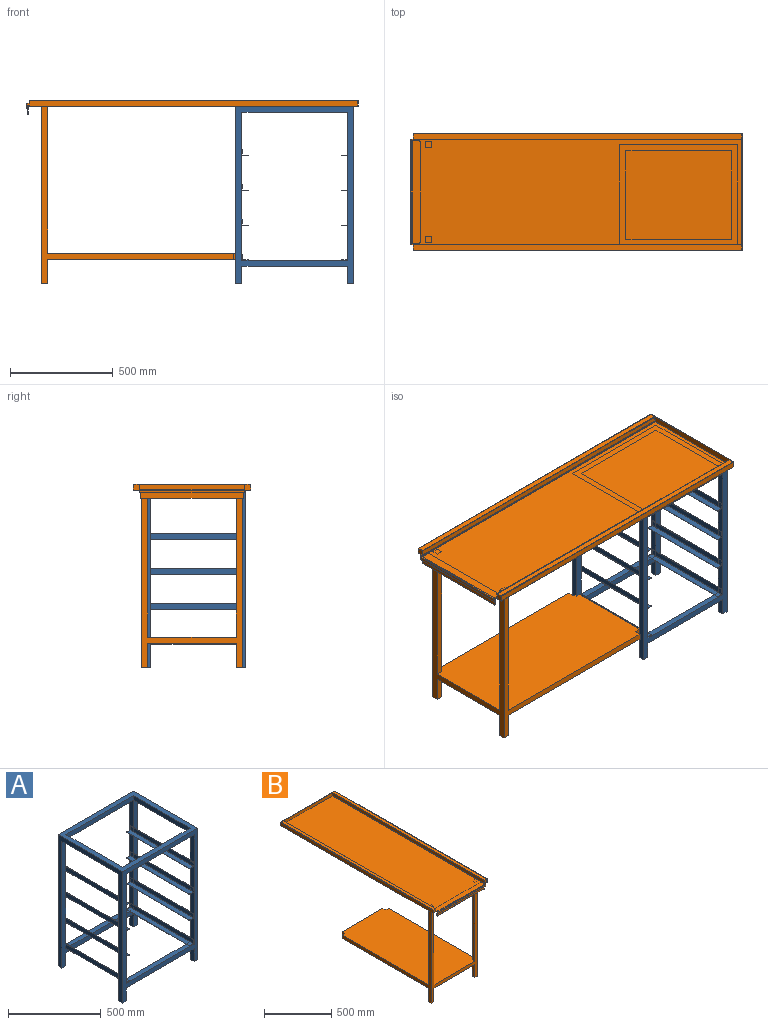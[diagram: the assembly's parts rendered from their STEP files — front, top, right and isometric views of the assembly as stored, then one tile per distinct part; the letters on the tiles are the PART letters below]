
ASSEMBLY  parts=2 mates=1
PART A: 127 faces, bbox 575x490x865 mm
  f0: plane 720x30mm, normal (-1,0,0), area 18621.5mm2, adj f3,f18,f20,f26,f82,f84,f90,f93
  f1: plane 515x30mm, normal (0,0,1), area 13960.7mm2, adj f5,f6,f8,f12,f35,f38,f39,f83
  f2: plane 720x30mm, normal (1,0,0), area 18621.5mm2, adj f3,f18,f20,f26,f34,f36,f42,f45
  f3: plane 515x30mm, normal (0,0,1), area 13960.7mm2, adj f0,f2,f18,f20,f36,f38,f40,f84
  f4: plane 515x30mm, normal (0,1,0), area 15450mm2, adj f10,f17,f28,f29
  f5: plane 835x575mm, normal (0,1,0), area 65550mm2, adj f1,f6,f7,f9,f11,f12,f13,f14
  f6: plane 720x30mm, normal (1,0,0), area 18621.5mm2, adj f1,f5,f8,f17,f34,f35,f41,f45
  f7: plane 865x490mm, normal (-1,0,0), area 64800mm2, adj f5,f8,f10,f11,f18,f20,f22,f27
  f8: plane 865x575mm, normal (0,-1,0), area 82800mm2, adj f1,f6,f7,f9,f10,f11,f12,f13
  f9: plane 85x30mm, normal (1,0,0), area 2550mm2, adj f5,f8,f11,f16
  f10: plane 575x490mm, normal (0,0,1), area 60300mm2, adj f4,f7,f8,f13,f20,f21,f28,f29
  f11: plane 30x30mm, normal (0,0,-1), area 900mm2, adj f5,f7,f8,f9
  f12: plane 720x30mm, normal (-1,0,0), area 18621.5mm2, adj f1,f5,f8,f17,f82,f83,f89,f93
  f13: plane 865x490mm, normal (1,0,0), area 64800mm2, adj f5,f8,f10,f15,f18,f20,f24,f30
  f14: plane 85x30mm, normal (-1,0,0), area 2550mm2, adj f5,f8,f15,f16
  f15: plane 30x30mm, normal (0,0,-1), area 900mm2, adj f5,f8,f13,f14
  f16: plane 515x30mm, normal (0,0,-1), area 15450mm2, adj f5,f8,f9,f14
  f17: plane 515x30mm, normal (0,0,-1), area 15450mm2, adj f4,f6,f8,f12
  f18: plane 835x575mm, normal (0,-1,0), area 65550mm2, adj f0,f2,f3,f7,f13,f19,f22,f23
  f19: plane 85x30mm, normal (1,0,0), area 2550mm2, adj f18,f20,f22,f25
  f20: plane 865x575mm, normal (0,1,0), area 82800mm2, adj f0,f2,f3,f7,f10,f13,f19,f22
  f21: plane 515x30mm, normal (0,-1,0), area 15450mm2, adj f10,f26,f28,f29
  f22: plane 30x30mm, normal (0,0,-1), area 900mm2, adj f7,f18,f19,f20
  f23: plane 85x30mm, normal (-1,0,0), area 2550mm2, adj f18,f20,f24,f25
  f24: plane 30x30mm, normal (0,0,-1), area 900mm2, adj f13,f18,f20,f23
  f25: plane 515x30mm, normal (0,0,-1), area 15450mm2, adj f18,f19,f20,f23
  f26: plane 515x30mm, normal (0,0,-1), area 15450mm2, adj f0,f2,f20,f21
  f27: plane 430x30mm, normal (0,0,-1), area 12900mm2, adj f5,f7,f18,f28
  f28: plane 430x30mm, normal (1,0,0), area 12900mm2, adj f4,f10,f21,f27
  f29: plane 430x30mm, normal (-1,0,0), area 12900mm2, adj f4,f10,f21,f30
  f30: plane 430x30mm, normal (0,0,-1), area 12900mm2, adj f5,f13,f18,f29
  f31: plane 430x30mm, normal (0,0,-1), area 12900mm2, adj f5,f18,f32,f38
  f32: plane 430x30mm, normal (-1,0,0), area 12900mm2, adj f5,f18,f31,f34
  f33: plane 480x28.5mm, normal (1,0,0), area 13669.3mm2, adj f34,f35,f36,f37,f41,f42
  f34: plane 470x1.5mm, normal (0,0,1), area 705mm2, adj f2,f6,f32,f33,f41,f42
  f35: plane 25x25mm, normal (0,-1,0), area 72.8mm2, adj f1,f6,f33,f37,f39,f41
  f36: plane 25x25mm, normal (0,1,0), area 72.8mm2, adj f2,f3,f33,f37,f40,f42
  f37: plane 480x28.5mm, normal (0,0,1), area 13669.3mm2, adj f33,f35,f36,f38,f39,f40
  f38: plane 470x1.5mm, normal (1,0,0), area 705mm2, adj f1,f3,f31,f37,f39,f40
  f39: cylinder r=5mm len=5mm, axis (0,0,1), area 11.8mm2, adj f1,f35,f37,f38
  f40: cylinder r=5mm len=5mm, axis (0,0,-1), area 11.8mm2, adj f3,f36,f37,f38
  f41: cylinder r=5mm len=5mm, axis (-1,0,0), area 11.8mm2, adj f6,f33,f34,f35
  f42: cylinder r=5mm len=5mm, axis (1,0,0), area 11.8mm2, adj f2,f33,f34,f36
  f43: plane 430x30mm, normal (-1,0,0), area 12900mm2, adj f5,f18,f45,f47
  f44: plane 480x28.5mm, normal (1,0,0), area 13669.3mm2, adj f45,f46,f48,f49,f53,f54
  f45: plane 470x1.5mm, normal (0,0,1), area 705mm2, adj f2,f6,f43,f44,f53,f54
  f46: plane 25x25mm, normal (0,-1,0), area 72.8mm2, adj f6,f44,f47,f49,f52,f54
  f47: plane 480x30mm, normal (0,0,-1), area 14389.3mm2, adj f2,f6,f43,f46,f48,f50,f51,f52
  f48: plane 25x25mm, normal (0,1,0), area 72.8mm2, adj f2,f44,f47,f49,f51,f53
  f49: plane 480x28.5mm, normal (0,0,1), area 13669.3mm2, adj f44,f46,f48,f50,f51,f52
  f50: plane 470x1.5mm, normal (1,0,0), area 705mm2, adj f47,f49,f51,f52
  f51: cylinder r=5mm len=5mm, axis (0,0,-1), area 11.8mm2, adj f47,f48,f49,f50
  f52: cylinder r=5mm len=5mm, axis (0,0,1), area 11.8mm2, adj f46,f47,f49,f50
  f53: cylinder r=5mm len=5mm, axis (1,0,0), area 11.8mm2, adj f2,f44,f45,f48
  f54: cylinder r=5mm len=5mm, axis (-1,0,0), area 11.8mm2, adj f6,f44,f45,f46
  f55: plane 430x30mm, normal (-1,0,0), area 12900mm2, adj f5,f18,f57,f59
  f56: plane 480x28.5mm, normal (1,0,0), area 13669.3mm2, adj f57,f58,f60,f61,f65,f66
  f57: plane 470x1.5mm, normal (0,0,1), area 705mm2, adj f2,f6,f55,f56,f65,f66
  f58: plane 25x25mm, normal (0,-1,0), area 72.8mm2, adj f6,f56,f59,f61,f64,f65
  f59: plane 480x30mm, normal (0,0,-1), area 14389.3mm2, adj f2,f6,f55,f58,f60,f62,f63,f64
  f60: plane 25x25mm, normal (0,1,0), area 72.8mm2, adj f2,f56,f59,f61,f63,f66
  f61: plane 480x28.5mm, normal (0,0,1), area 13669.3mm2, adj f56,f58,f60,f62,f63,f64
  f62: plane 470x1.5mm, normal (1,0,0), area 705mm2, adj f59,f61,f63,f64
  f63: cylinder r=5mm len=5mm, axis (0,0,-1), area 11.8mm2, adj f59,f60,f61,f62
  f64: cylinder r=5mm len=5mm, axis (0,0,1), area 11.8mm2, adj f58,f59,f61,f62
  f65: cylinder r=5mm len=5mm, axis (-1,0,0), area 11.8mm2, adj f6,f56,f57,f58
  f66: cylinder r=5mm len=5mm, axis (1,0,0), area 11.8mm2, adj f2,f56,f57,f60
  f67: plane 430x30mm, normal (-1,0,0), area 12900mm2, adj f5,f18,f69,f71
  f68: plane 480x28.5mm, normal (1,0,0), area 13669.3mm2, adj f69,f70,f72,f73,f77,f78
  f69: plane 470x1.5mm, normal (0,0,1), area 705mm2, adj f2,f6,f67,f68,f77,f78
  f70: plane 25x25mm, normal (0,-1,0), area 72.7mm2, adj f6,f68,f71,f73,f76,f77
  f71: plane 480x30mm, normal (0,0,-1), area 14389.3mm2, adj f2,f6,f67,f70,f72,f74,f75,f76
  f72: plane 25x25mm, normal (0,1,0), area 72.7mm2, adj f2,f68,f71,f73,f75,f78
  f73: plane 480x28.5mm, normal (0,0,1), area 13669.3mm2, adj f68,f70,f72,f74,f75,f76
  f74: plane 470x1.5mm, normal (1,0,0), area 705mm2, adj f71,f73,f75,f76
  f75: cylinder r=5mm len=5mm, axis (0,0,-1), area 11.8mm2, adj f71,f72,f73,f74
  f76: cylinder r=5mm len=5mm, axis (0,0,1), area 11.8mm2, adj f70,f71,f73,f74
  f77: cylinder r=5mm len=5mm, axis (-1,0,0), area 11.8mm2, adj f6,f68,f69,f70
  f78: cylinder r=5mm len=5mm, axis (1,0,0), area 11.8mm2, adj f2,f68,f69,f72
  f79: plane 430x30mm, normal (0,0,-1), area 12900mm2, adj f5,f18,f80,f86
  f80: plane 430x30mm, normal (1,0,0), area 12900mm2, adj f5,f18,f79,f82
  f81: plane 480x28.5mm, normal (-1,0,0), area 13669.3mm2, adj f82,f83,f84,f85,f89,f90
  f82: plane 470x1.5mm, normal (0,0,1), area 705mm2, adj f0,f12,f80,f81,f89,f90
  f83: plane 25x25mm, normal (0,-1,0), area 72.8mm2, adj f1,f12,f81,f85,f87,f89
  f84: plane 25x25mm, normal (0,1,0), area 72.8mm2, adj f0,f3,f81,f85,f88,f90
  f85: plane 480x28.5mm, normal (0,0,1), area 13669.3mm2, adj f81,f83,f84,f86,f87,f88
  f86: plane 470x1.5mm, normal (-1,0,0), area 705mm2, adj f1,f3,f79,f85,f87,f88
  f87: cylinder r=5mm len=5mm, axis (0,0,1), area 11.8mm2, adj f1,f83,f85,f86
  f88: cylinder r=5mm len=5mm, axis (0,0,-1), area 11.8mm2, adj f3,f84,f85,f86
  f89: cylinder r=5mm len=5mm, axis (1,0,0), area 11.8mm2, adj f12,f81,f82,f83
  f90: cylinder r=5mm len=5mm, axis (-1,0,0), area 11.8mm2, adj f0,f81,f82,f84
  f91: plane 430x30mm, normal (1,0,0), area 12900mm2, adj f5,f18,f93,f95
  f92: plane 480x28.5mm, normal (-1,0,0), area 13669.3mm2, adj f93,f94,f96,f97,f101,f102
  f93: plane 470x1.5mm, normal (0,0,1), area 705mm2, adj f0,f12,f91,f92,f101,f102
  f94: plane 25x25mm, normal (0,-1,0), area 72.8mm2, adj f12,f92,f95,f97,f100,f102
  f95: plane 480x30mm, normal (0,0,-1), area 14389.3mm2, adj f0,f12,f91,f94,f96,f98,f99,f100
  f96: plane 25x25mm, normal (0,1,0), area 72.8mm2, adj f0,f92,f95,f97,f99,f101
  f97: plane 480x28.5mm, normal (0,0,1), area 13669.3mm2, adj f92,f94,f96,f98,f99,f100
  f98: plane 470x1.5mm, normal (-1,0,0), area 705mm2, adj f95,f97,f99,f100
  f99: cylinder r=5mm len=5mm, axis (0,0,-1), area 11.8mm2, adj f95,f96,f97,f98
  f100: cylinder r=5mm len=5mm, axis (0,0,1), area 11.8mm2, adj f94,f95,f97,f98
  f101: cylinder r=5mm len=5mm, axis (-1,0,0), area 11.8mm2, adj f0,f92,f93,f96
  f102: cylinder r=5mm len=5mm, axis (1,0,0), area 11.8mm2, adj f12,f92,f93,f94
  f103: plane 430x30mm, normal (1,0,0), area 12900mm2, adj f5,f18,f105,f107
  f104: plane 480x28.5mm, normal (-1,0,0), area 13669.3mm2, adj f105,f106,f108,f109,f113,f114
  f105: plane 470x1.5mm, normal (0,0,1), area 705mm2, adj f0,f12,f103,f104,f113,f114
  f106: plane 25x25mm, normal (0,-1,0), area 72.8mm2, adj f12,f104,f107,f109,f112,f113
  f107: plane 480x30mm, normal (0,0,-1), area 14389.3mm2, adj f0,f12,f103,f106,f108,f110,f111,f112
  f108: plane 25x25mm, normal (0,1,0), area 72.8mm2, adj f0,f104,f107,f109,f111,f114
  f109: plane 480x28.5mm, normal (0,0,1), area 13669.3mm2, adj f104,f106,f108,f110,f111,f112
  f110: plane 470x1.5mm, normal (-1,0,0), area 705mm2, adj f107,f109,f111,f112
  f111: cylinder r=5mm len=5mm, axis (0,0,-1), area 11.8mm2, adj f107,f108,f109,f110
  f112: cylinder r=5mm len=5mm, axis (0,0,1), area 11.8mm2, adj f106,f107,f109,f110
  f113: cylinder r=5mm len=5mm, axis (1,0,0), area 11.8mm2, adj f12,f104,f105,f106
  f114: cylinder r=5mm len=5mm, axis (-1,0,0), area 11.8mm2, adj f0,f104,f105,f108
  f115: plane 430x30mm, normal (1,0,0), area 12900mm2, adj f5,f18,f117,f119
  f116: plane 480x28.5mm, normal (-1,0,0), area 13669.3mm2, adj f117,f118,f120,f121,f125,f126
  f117: plane 470x1.5mm, normal (0,0,1), area 705mm2, adj f0,f12,f115,f116,f125,f126
  f118: plane 25x25mm, normal (0,-1,0), area 72.7mm2, adj f12,f116,f119,f121,f124,f125
  f119: plane 480x30mm, normal (0,0,-1), area 14389.3mm2, adj f0,f12,f115,f118,f120,f122,f123,f124
  f120: plane 25x25mm, normal (0,1,0), area 72.7mm2, adj f0,f116,f119,f121,f123,f126
  f121: plane 480x28.5mm, normal (0,0,1), area 13669.3mm2, adj f116,f118,f120,f122,f123,f124
  f122: plane 470x1.5mm, normal (-1,0,0), area 705mm2, adj f119,f121,f123,f124
  f123: cylinder r=5mm len=5mm, axis (0,0,-1), area 11.8mm2, adj f119,f120,f121,f122
  f124: cylinder r=5mm len=5mm, axis (0,0,1), area 11.8mm2, adj f118,f119,f121,f122
  f125: cylinder r=5mm len=5mm, axis (1,0,0), area 11.8mm2, adj f12,f116,f117,f118
  f126: cylinder r=5mm len=5mm, axis (-1,0,0), area 11.8mm2, adj f0,f116,f117,f120
PART B: 74 faces, bbox 570x1616.5x895.5 mm
  f0: plane 30x30mm, normal (0,1,0), area 900mm2, adj f66,f68,f69,f72
  f1: plane 715.5x30mm, normal (0,1,0), area 21465mm2, adj f2,f5,f59,f68
  f2: plane 715.5x30mm, normal (1,0,0), area 21465mm2, adj f1,f5,f62,f68
  f3: plane 715.5x30mm, normal (-1,0,0), area 21465mm2, adj f4,f5,f62,f68
  f4: plane 715.5x30mm, normal (0,1,0), area 21465mm2, adj f3,f5,f66,f68
  f5: plane 1615x570mm, normal (0,0,-1), area 802000.2mm2, adj f1,f2,f3,f4,f9,f10,f11,f14
  f6: plane 500x38.5mm, normal (0,0,-1), area 19239.3mm2, adj f49,f50,f51,f53,f54,f55
  f7: plane 13.5x12mm, normal (-1,0,0), area 162mm2, adj f9,f17,f39,f40
  f8: plane 1598.5x25.5mm, normal (-1,0,0), area 40761.8mm2, adj f10,f31,f35,f48
  f9: cylinder r=3mm len=13.5mm, axis (0,1,0), area 63.6mm2, adj f5,f7,f17,f40
  f10: cylinder r=3mm len=1598.5mm, axis (0,1,0), area 7532.8mm2, adj f5,f8,f35,f48
  f11: plane 1598.5x28.5mm, normal (-1,0,0), area 45557.3mm2, adj f5,f13,f34,f47
  f12: plane 13.5x12mm, normal (1,0,0), area 162mm2, adj f14,f15,f16,f38
  f13: plane 1598.5x27mm, normal (0,0,-1), area 43159.5mm2, adj f11,f33,f34,f47
  f14: cylinder r=3mm len=13.5mm, axis (0,1,0), area 63.6mm2, adj f5,f12,f15,f16
  f15: plane 15x3mm, normal (0,-1,0), area 23.3mm2, adj f12,f14,f21,f22,f38,f41
  f16: plane 31.5x30mm, normal (0,-1,0), area 878.5mm2, adj f5,f12,f14,f18,f19,f20,f21,f27
  f17: plane 31.5x30mm, normal (0,-1,0), area 878.5mm2, adj f5,f7,f9,f25,f26,f27,f28,f29
  f18: plane 1601.5x28.5mm, normal (1,0,0), area 45642.8mm2, adj f5,f16,f19,f36
  f19: cylinder r=1.5mm len=1601.5mm, axis (0,1,0), area 3773.4mm2, adj f16,f18,f27,f36
  f20: cylinder r=1.5mm len=1600mm, axis (0,1,0), area 3769.9mm2, adj f16,f21,f27,f37
  f21: plane 1613.5x25.5mm, normal (-1,0,0), area 40962mm2, adj f15,f16,f20,f22,f37,f38
  f22: cylinder r=1.5mm len=1613.5mm, axis (0,1,0), area 3801.7mm2, adj f15,f21,f23,f37
  f23: plane 1613.5x507mm, normal (0,0,1), area 818044.5mm2, adj f22,f24,f37,f42
  f24: cylinder r=1.5mm len=1613.5mm, axis (0,1,0), area 3801.7mm2, adj f23,f25,f37,f40
  f25: plane 1613.5x25.5mm, normal (1,0,0), area 40962mm2, adj f17,f24,f26,f37,f39,f40
  f26: cylinder r=1.5mm len=1600mm, axis (0,1,0), area 3769.9mm2, adj f17,f25,f27,f37
  f27: plane 1601.5x567mm, normal (0,0,1), area 87250.5mm2, adj f16,f17,f19,f20,f26,f28,f36,f37
  f28: cylinder r=1.5mm len=1601.5mm, axis (0,1,0), area 3773.4mm2, adj f17,f27,f29,f36
  f29: plane 1601.5x28.5mm, normal (-1,0,0), area 45642.8mm2, adj f5,f17,f28,f36
  f30: plane 1598.5x28.5mm, normal (1,0,0), area 45557.3mm2, adj f5,f31,f35,f48
  f31: plane 1598.5x27mm, normal (0,0,-1), area 43159.5mm2, adj f8,f30,f35,f48
  f32: cylinder r=3mm len=1598.5mm, axis (0,1,0), area 7532.8mm2, adj f5,f33,f34,f47
  f33: plane 1598.5x25.5mm, normal (1,0,0), area 40761.8mm2, adj f13,f32,f34,f47
  f34: plane 30x28.5mm, normal (0,-1,0), area 771.4mm2, adj f5,f11,f13,f32,f33
  f35: plane 30x28.5mm, normal (0,-1,0), area 771.4mm2, adj f5,f8,f10,f30,f31
  f36: plane 570x30mm, normal (0,1,0), area 17099mm2, adj f5,f18,f19,f27,f28,f29
  f37: plane 513x28.5mm, normal (0,-1,0), area 14535mm2, adj f20,f21,f22,f23,f24,f25,f26,f27
  f38: plane 13.5x1.5mm, normal (0,0,1), area 20.2mm2, adj f12,f15,f16,f21
  f39: plane 13.5x1.5mm, normal (0,0,1), area 20.2mm2, adj f7,f17,f25,f40
  f40: plane 15x3mm, normal (0,-1,0), area 23.3mm2, adj f7,f9,f24,f25,f39,f43
  f41: plane 15x1.5mm, normal (1,0,0), area 22mm2, adj f15,f42,f44,f45,f46
  f42: cylinder r=1.5mm len=507mm, axis (-1,0,0), area 1194.6mm2, adj f23,f41,f43,f45
  f43: plane 15x1.5mm, normal (-1,0,0), area 22mm2, adj f40,f42,f44,f45,f46
  f44: plane 507x13.5mm, normal (0,1,0), area 6844.5mm2, adj f5,f41,f43,f46
  f45: plane 507x13.5mm, normal (0,-1,0), area 6844.5mm2, adj f41,f42,f43,f46
  f46: plane 507x1.5mm, normal (0,0,-1), area 760.5mm2, adj f41,f43,f44,f45
  f47: plane 30x28.5mm, normal (0,1,0), area 771.4mm2, adj f5,f11,f13,f32,f33
  f48: plane 30x28.5mm, normal (0,1,0), area 771.4mm2, adj f5,f8,f10,f30,f31
  f49: plane 490x1.5mm, normal (0,1,0), area 735mm2, adj f5,f6,f50,f54
  f50: cylinder r=5mm len=5mm, axis (0,0,1), area 11.8mm2, adj f5,f6,f49,f51
  f51: plane 35x35mm, normal (1,0,0), area 102.7mm2, adj f5,f6,f50,f52,f55,f57
  f52: plane 500x40mm, normal (0,-1,0), area 19989.3mm2, adj f5,f51,f53,f56,f57,f58
  f53: plane 35x35mm, normal (-1,0,0), area 102.7mm2, adj f5,f6,f52,f54,f55,f58
  f54: cylinder r=5mm len=5mm, axis (0,0,1), area 11.8mm2, adj f5,f6,f49,f53
  f55: plane 500x38.5mm, normal (0,1,0), area 19239.3mm2, adj f6,f51,f53,f56,f57,f58
  f56: plane 490x1.5mm, normal (0,0,-1), area 735mm2, adj f52,f55,f57,f58
  f57: cylinder r=5mm len=5mm, axis (0,1,0), area 11.8mm2, adj f51,f52,f55,f56
  f58: cylinder r=5mm len=5mm, axis (0,-1,0), area 11.8mm2, adj f52,f53,f55,f56
  f59: plane 936.5x865.5mm, normal (-1,0,0), area 53160mm2, adj f1,f5,f60,f62,f63,f68,f69,f70
  f60: plane 120x30mm, normal (0,1,0), area 3600mm2, adj f59,f61,f63,f69
  f61: plane 120x30mm, normal (1,0,0), area 3600mm2, adj f60,f62,f63,f69
  f62: plane 865.5x490mm, normal (0,-1,0), area 64830mm2, adj f2,f3,f5,f59,f61,f63,f64,f66
  f63: plane 30x30mm, normal (0,0,-1), area 900mm2, adj f59,f60,f61,f62
  f64: plane 120x30mm, normal (-1,0,0), area 3600mm2, adj f62,f65,f67,f69
  f65: plane 120x30mm, normal (0,1,0), area 3600mm2, adj f64,f66,f67,f69
  f66: plane 936.5x865.5mm, normal (1,0,0), area 53160mm2, adj f0,f4,f5,f62,f65,f67,f68,f69
  f67: plane 30x30mm, normal (0,0,-1), area 900mm2, adj f62,f64,f65,f66
  f68: plane 966.5x490mm, normal (0,0,1), area 469985mm2, adj f0,f1,f2,f3,f4,f59,f62,f66
  f69: plane 966.5x490mm, normal (0,0,-1), area 469985mm2, adj f0,f59,f60,f61,f62,f64,f65,f66
  f70: plane 30x30mm, normal (0,1,0), area 900mm2, adj f59,f68,f69,f71
  f71: plane 30x30mm, normal (-1,0,0), area 900mm2, adj f68,f69,f70,f73
  f72: plane 30x30mm, normal (1,0,0), area 900mm2, adj f0,f68,f69,f73
  f73: plane 430x30mm, normal (0,1,0), area 12900mm2, adj f68,f69,f71,f72
PLACE A t=(-324.78,-0.53,-137.02)mm
PLACE B rot(axis=(0,0,-1),90deg) t=(-18.78,14.47,727.98)mm
MATE fastened B.f5 <-> A.f10  axis (0,0,-1) through (-17.28,-270.53,727.98)mm
